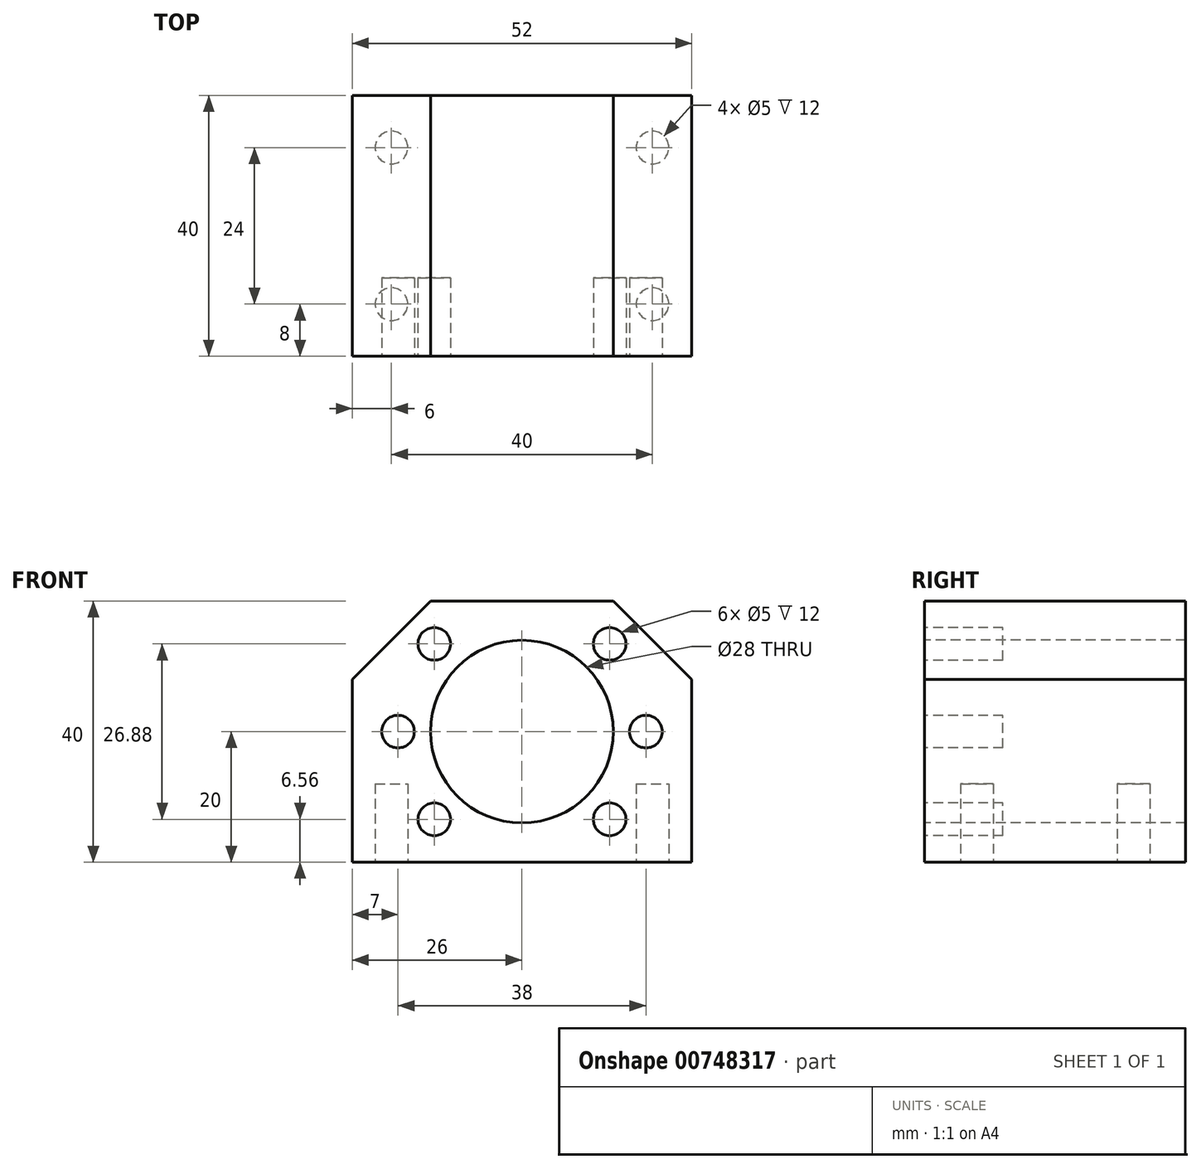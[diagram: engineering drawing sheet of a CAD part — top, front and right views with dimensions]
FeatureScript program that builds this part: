
annotation { "Feature Type Name" : "Feature", "Feature Type Description" : "" }
export const myFeature = defineFeature(function(context is Context, id is Id, definition is map)
    precondition{}
    {
        {
            var Q0;
            Q0=qCreatedBy(makeId("Front.planeOp"),FACE);
            var sketch = newSketch(context, id + "F0", { "sketchPlane" : qUnion([Q0])});
            skLineSegment(sketch, "E0.bottom", {"start": v(26, -20) * mm, "end": v(-26, -20) * mm});
            skLineSegment(sketch, "E0.top", {"start": v(26, 20) * mm, "end": v(-26, 20) * mm});
            skLineSegment(sketch, "E0.left", {"start": v(26, -20) * mm, "end": v(26, 20) * mm});
            skLineSegment(sketch, "E0.right", {"start": v(-26, -20) * mm, "end": v(-26, 20) * mm});
            skPoint(sketch, "E0.middle", {"position": v(0, 0) * mm});
            skSolve(sketch);
        }
        {
            var Q0;
            Q0 = qSketchRegion(id + "F0", true);
            extrude(context, id + "F1", {"entities" : qUnion([Q0]), "depth" : 40 * mm, "offsetDistance" : 25.4 * mm});
        }
        {
            var Q0;
            Q0=makeQuery(id+"F1.opExtrude","CAP_FACE",FACE,{"disambiguationData":[OSD([sQuery(id+"F0.wireOp",EDGE,"E0.bottom"),sQuery(id+"F0.wireOp",EDGE,"E0.top"),sQuery(id+"F0.wireOp",EDGE,"E0.left"),sQuery(id+"F0.wireOp",EDGE,"E0.right")])],"isStart":false});
            var sketch = newSketch(context, id + "F2", { "sketchPlane" : qUnion([Q0])});
            skCircle(sketch, "E1", {"center": v(0, 0) * mm, "radius": 14 * mm});
            skSolve(sketch);
        }
        {
            var Q0;
            Q0=makeQuery(id+"F2.imprint","IMPRINT",FACE,{"disambiguationData":[TD([[makeQuery(id+"F2.imprint","IMPRINT",EDGE,{"derivedFrom":sQuery(id+"F2.wireOp",EDGE,"E1")}),1.0]])]});
            extrude(context, id + "F3", {"entities" : qUnion([Q0]), "operationType" : NewBodyOperationType.REMOVE, "endBound" : BoundingType.THROUGH_ALL, "oppositeDirection" : true, "depth" : 25.4 * mm, "offsetDistance" : 25.4 * mm});
        }
        {
            var Q0;
            Q0=makeQuery(id+"F1.opExtrude","SWEPT_EDGE",EDGE,{"disambiguationData":[OSD([sQuery(id+"F0.wireOp",EDGE,"E0.top"),sQuery(id+"F0.wireOp",EDGE,"E0.right")])]});
            var Q1;
            Q1=makeQuery(id+"F1.opExtrude","SWEPT_EDGE",EDGE,{"disambiguationData":[OSD([sQuery(id+"F0.wireOp",EDGE,"E0.top"),sQuery(id+"F0.wireOp",EDGE,"E0.left")])]});
            chamfer(context, id + "F4", {"entities" : qUnion([Q0, Q1]), "width" : 12 * mm, "tangentPropagation" : true});
        }
        {
            var Q0;
            Q0=makeQuery(id+"F1.opExtrude","SWEPT_FACE",FACE,{"disambiguationData":[OSD([sQuery(id+"F0.wireOp",EDGE,"E0.bottom")])]});
            var sketch = newSketch(context, id + "F5", { "sketchPlane" : qUnion([Q0])});
            skSolve(sketch);
        }
        {
            var Q0;
            Q0=makeQuery(id+"F1.opExtrude","CAP_FACE",FACE,{"disambiguationData":[OSD([sQuery(id+"F0.wireOp",EDGE,"E0.bottom"),sQuery(id+"F0.wireOp",EDGE,"E0.top"),sQuery(id+"F0.wireOp",EDGE,"E0.left"),sQuery(id+"F0.wireOp",EDGE,"E0.right")])],"isStart":false});
            var sketch = newSketch(context, id + "F6", { "sketchPlane" : qUnion([Q0])});
            skCircle(sketch, "E2", {"center": v(0, 0) * mm, "radius": 19 * mm, "construction": true});
            skCircle(sketch, "E3", {"center": v(-19, 0) * mm, "radius": 2.5 * mm});
            skCircle(sketch, "E4.1.0", {"center": v(-13.44, -13.44) * mm, "radius": 2.5 * mm});
            skCircle(sketch, "E4.3.0", {"center": v(13.44, -13.44) * mm, "radius": 2.5 * mm});
            skCircle(sketch, "E4.4.0", {"center": v(19, 0) * mm, "radius": 2.5 * mm});
            skCircle(sketch, "E4.5.0", {"center": v(13.44, 13.44) * mm, "radius": 2.5 * mm});
            skCircle(sketch, "E4.7.0", {"center": v(-13.44, 13.44) * mm, "radius": 2.5 * mm});
            skLineSegment(sketch, "E5", {"start": v(0, 0) * mm, "end": v(-19, 0) * mm, "construction": true});
            skLineSegment(sketch, "E6", {"start": v(0, 0) * mm, "end": v(-13.44, 13.44) * mm, "construction": true});
            skSolve(sketch);
        }
        {
            var Q0;
            Q0 = qSketchRegion(id + "F6", true);
            extrude(context, id + "F7", {"entities" : qUnion([Q0]), "operationType" : NewBodyOperationType.REMOVE, "oppositeDirection" : true, "depth" : 12 * mm, "offsetDistance" : 25.4 * mm});
        }
        {
            var Q0;
            {var subQ0=sQuery(id+"F0.wireOp",EDGE,"E0.bottom");Q0=makeQuery(id+"F5.imprint","IMPRINT",FACE,{"disambiguationData":[TD([[makeQuery(id+"F5.imprint","IMPRINT",EDGE,{"derivedFrom":makeQuery(id+"F1.opExtrude","CAP_EDGE",EDGE,{"disambiguationData":[OSD([subQ0])],"isStart":true})}),-1.0]])]});}
            var sketch = newSketch(context, id + "F8", { "sketchPlane" : qUnion([Q0])});
            skLineSegment(sketch, "E7", {"start": v(0, 0) * mm, "end": v(0, 40) * mm, "construction": true});
            skLineSegment(sketch, "E8.bottom", {"start": v(20, 8) * mm, "end": v(-20, 8) * mm, "construction": true});
            skLineSegment(sketch, "E8.top", {"start": v(20, 32) * mm, "end": v(-20, 32) * mm, "construction": true});
            skLineSegment(sketch, "E8.left", {"start": v(20, 8) * mm, "end": v(20, 32) * mm, "construction": true});
            skLineSegment(sketch, "E8.right", {"start": v(-20, 8) * mm, "end": v(-20, 32) * mm, "construction": true});
            skPoint(sketch, "E8.middle", {"position": v(0, 20) * mm});
            skCircle(sketch, "E9", {"center": v(-20, 32) * mm, "radius": 2.5 * mm});
            skCircle(sketch, "E10", {"center": v(20, 32) * mm, "radius": 2.5 * mm});
            skCircle(sketch, "E11", {"center": v(20, 8) * mm, "radius": 2.5 * mm});
            skCircle(sketch, "E12", {"center": v(-20, 8) * mm, "radius": 2.5 * mm});
            skSolve(sketch);
        }
        {
            var Q0;
            Q0 = qSketchRegion(id + "F8", true);
            extrude(context, id + "F9", {"entities" : qUnion([Q0]), "operationType" : NewBodyOperationType.REMOVE, "oppositeDirection" : true, "depth" : 12 * mm, "offsetDistance" : 25.4 * mm});
        }
    });
